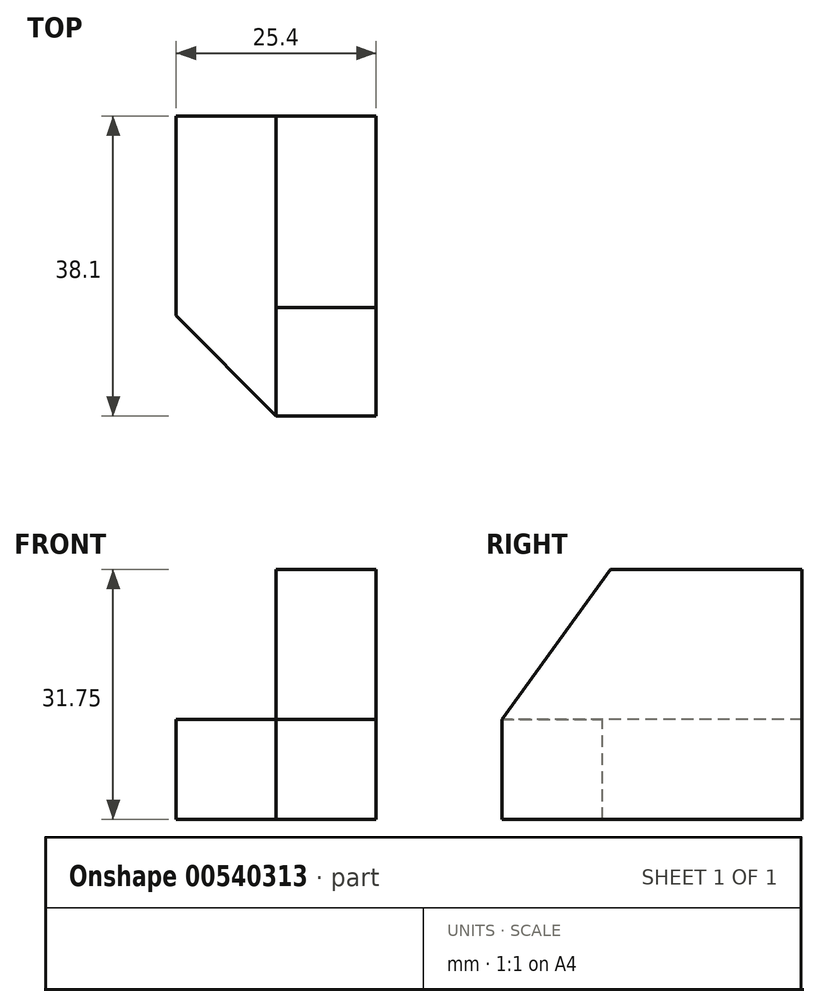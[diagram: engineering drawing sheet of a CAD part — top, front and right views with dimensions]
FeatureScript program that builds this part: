
annotation { "Feature Type Name" : "Feature", "Feature Type Description" : "" }
export const myFeature = defineFeature(function(context is Context, id is Id, definition is map)
    precondition{}
    {
        {
            var Q0;
            Q0=qCreatedBy(makeId("Front.planeOp"),FACE);
            var sketch = newSketch(context, id + "F0", { "sketchPlane" : qUnion([Q0])});
            skLineSegment(sketch, "E0", {"start": v(-25.4, 31.75) * mm, "end": v(-25.4, 0) * mm});
            skLineSegment(sketch, "E1", {"start": v(-25.4, 0) * mm, "end": v(0, 0) * mm});
            skLineSegment(sketch, "E2", {"start": v(0, 0) * mm, "end": v(0, 31.75) * mm});
            skLineSegment(sketch, "E3", {"start": v(-25.4, 31.75) * mm, "end": v(0, 31.75) * mm});
            skSolve(sketch);
        }
        {
            var Q0;
            Q0 = qSketchRegion(id + "F0", true);
            extrude(context, id + "F1", {"entities" : qUnion([Q0]), "depth" : 38.1 * mm, "offsetDistance" : 25.4 * mm});
        }
        {
            var Q0;
            Q0=makeQuery(id+"F1.opExtrude","CAP_FACE",FACE,{"disambiguationData":[OSD([sQuery(id+"F0.wireOp",EDGE,"E0"),sQuery(id+"F0.wireOp",EDGE,"E1"),sQuery(id+"F0.wireOp",EDGE,"E2"),sQuery(id+"F0.wireOp",EDGE,"E3")])],"isStart":false});
            var sketch = newSketch(context, id + "F2", { "sketchPlane" : qUnion([Q0])});
            skLineSegment(sketch, "E4", {"start": v(-12.7, 31.75) * mm, "end": v(-12.7, 12.7) * mm});
            skPoint(sketch, "E4.endSnap0", {"position": v(-12.7, 31.75) * mm});
            skLineSegment(sketch, "E5", {"start": v(-12.7, 12.7) * mm, "end": v(-25.4, 12.7) * mm});
            skSolve(sketch);
        }
        {
            var Q0;
            {var subQ0=sQuery(id+"F2.wireOp",EDGE,"E4");Q0=makeQuery(id+"F2.imprint","IMPRINT",FACE,{"disambiguationData":[TD([[makeQuery(id+"F2.imprint","IMPRINT",EDGE,{"derivedFrom":subQ0}),-1.0]])]});}
            extrude(context, id + "F3", {"entities" : qUnion([Q0]), "operationType" : NewBodyOperationType.REMOVE, "oppositeDirection" : true, "depth" : 38.1 * mm, "offsetDistance" : 25.4 * mm});
        }
        {
            var Q0;
            Q0=makeQuery(id+"F3.boolean.opBoolean","COPY",FACE,{"derivedFrom":makeQuery(id+"F3.opExtrude","SWEPT_FACE",FACE,{"disambiguationData":[OSD([sQuery(id+"F2.wireOp",EDGE,"E5")])]})});
            var sketch = newSketch(context, id + "F4", { "sketchPlane" : qUnion([Q0])});
            skLineSegment(sketch, "E6", {"start": v(-12.7, -38.1) * mm, "end": v(-25.4, -25.33) * mm});
            skSolve(sketch);
        }
        {
            var Q0;
            {var subQ0=sQuery(id+"F4.wireOp",EDGE,"E6");Q0=makeQuery(id+"F4.imprint","IMPRINT",FACE,{"disambiguationData":[TD([[makeQuery(id+"F4.imprint","IMPRINT",EDGE,{"derivedFrom":subQ0}),1.0]])]});}
            extrude(context, id + "F5", {"entities" : qUnion([Q0]), "operationType" : NewBodyOperationType.REMOVE, "oppositeDirection" : true, "depth" : 25.4 * mm, "offsetDistance" : 25.4 * mm});
        }
        {
            var Q0;
            Q0=makeQuery(id+"F3.boolean.opBoolean","COPY",FACE,{"derivedFrom":makeQuery(id+"F3.opExtrude","SWEPT_FACE",FACE,{"disambiguationData":[OSD([sQuery(id+"F2.wireOp",EDGE,"E4")])]})});
            var sketch = newSketch(context, id + "F6", { "sketchPlane" : qUnion([Q0])});
            skLineSegment(sketch, "E7", {"start": v(38.1, 12.7) * mm, "end": v(24.32, 31.75) * mm});
            skSolve(sketch);
        }
        {
            var Q0;
            {var subQ0=sQuery(id+"F6.wireOp",EDGE,"E7");Q0=makeQuery(id+"F6.imprint","IMPRINT",FACE,{"disambiguationData":[TD([[makeQuery(id+"F6.imprint","IMPRINT",EDGE,{"derivedFrom":subQ0}),-1.0]])]});}
            extrude(context, id + "F7", {"entities" : qUnion([Q0]), "operationType" : NewBodyOperationType.REMOVE, "oppositeDirection" : true, "depth" : 25.4 * mm, "offsetDistance" : 25.4 * mm});
        }
    });
